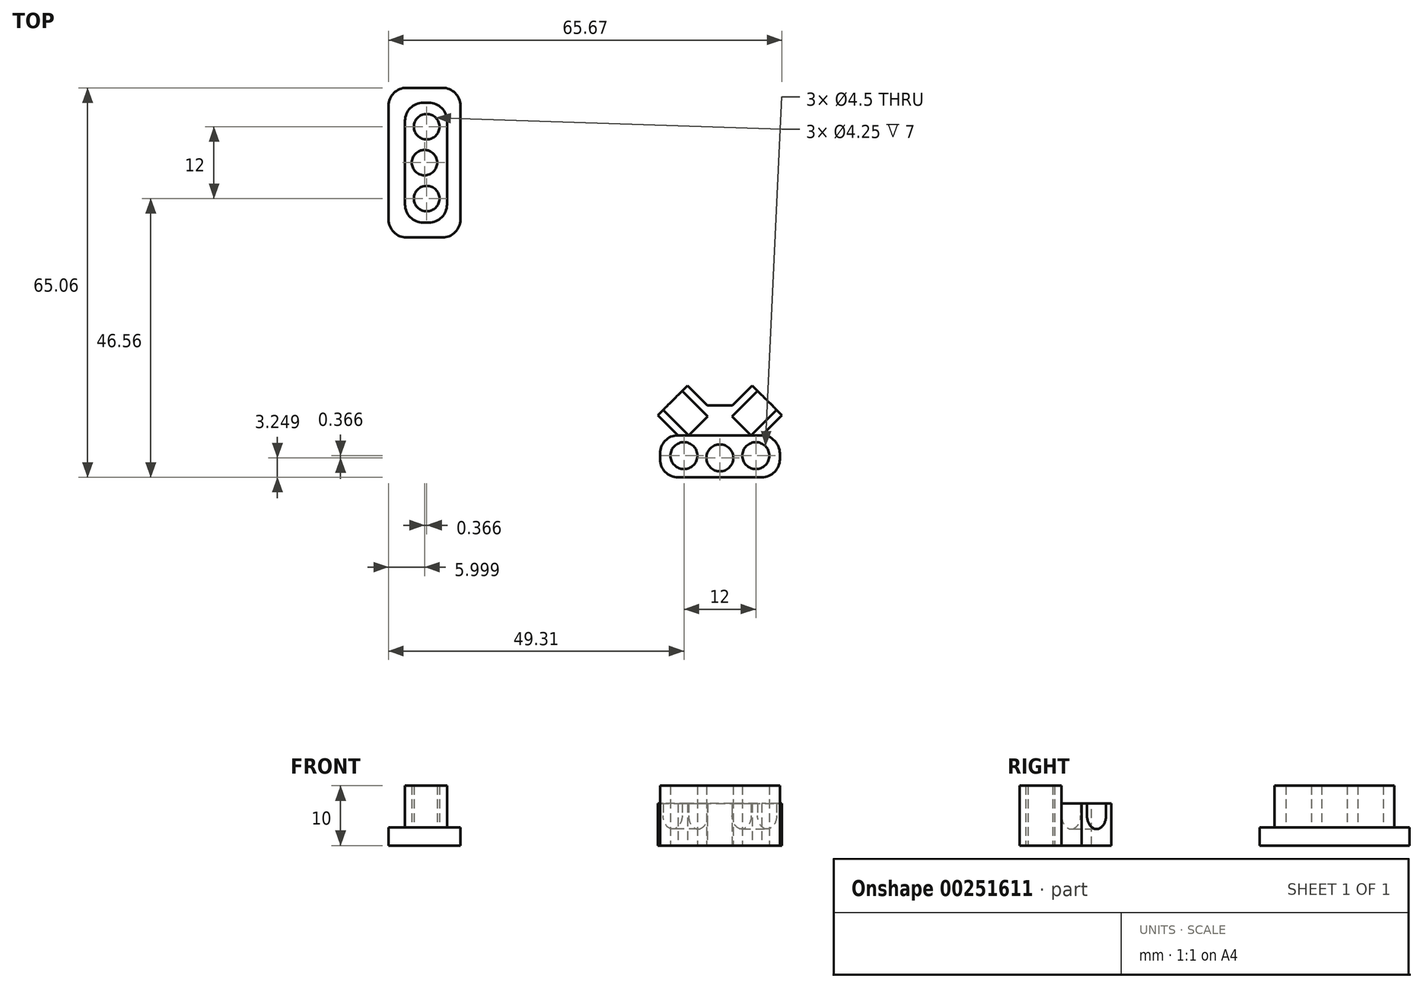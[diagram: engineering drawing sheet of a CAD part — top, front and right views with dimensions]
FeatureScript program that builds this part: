
annotation { "Feature Type Name" : "Feature", "Feature Type Description" : "" }
export const myFeature = defineFeature(function(context is Context, id is Id, definition is map)
    precondition{}
    {
        {
            var Q0;
            Q0=qCreatedBy(makeId("Top.planeOp"),FACE);
            var sketch = newSketch(context, id + "F0", { "sketchPlane" : qUnion([Q0])});
            skCircle(sketch, "E0.cCircle", {"center": v(0, 0) * mm, "radius": 49.31 * mm, "construction": true});
            skLineSegment(sketch, "E0.0", {"start": v(-45.56, 18.87) * mm, "end": v(-18.87, 45.56) * mm, "construction": true});
            skLineSegment(sketch, "E0.1", {"start": v(-18.87, 45.56) * mm, "end": v(18.87, 45.56) * mm, "construction": true});
            skLineSegment(sketch, "E0.2", {"start": v(18.87, 45.56) * mm, "end": v(45.56, 18.87) * mm, "construction": true});
            skLineSegment(sketch, "E0.3", {"start": v(45.56, 18.87) * mm, "end": v(45.56, -18.87) * mm, "construction": true});
            skLineSegment(sketch, "E0.4", {"start": v(45.56, -18.87) * mm, "end": v(18.87, -45.56) * mm, "construction": true});
            skLineSegment(sketch, "E0.5", {"start": v(18.87, -45.56) * mm, "end": v(-18.87, -45.56) * mm, "construction": true});
            skLineSegment(sketch, "E0.6", {"start": v(-18.87, -45.56) * mm, "end": v(-45.56, -18.87) * mm, "construction": true});
            skLineSegment(sketch, "E0.7", {"start": v(-45.56, -18.87) * mm, "end": v(-45.56, 18.87) * mm, "construction": true});
            skLineSegment(sketch, "E1.bottom", {"start": v(-48.56, -10) * mm, "end": v(-49.56, -10) * mm});
            skLineSegment(sketch, "E1.top", {"start": v(-48.56, 10) * mm, "end": v(-49.56, 10) * mm});
            skLineSegment(sketch, "E1.left", {"start": v(-45.56, -7) * mm, "end": v(-45.56, 7) * mm});
            skLineSegment(sketch, "E1.right", {"start": v(-52.56, -7) * mm, "end": v(-52.56, 7) * mm});
            skCircle(sketch, "E2", {"center": v(0, 0) * mm, "radius": 53.5 * mm, "construction": true});
            skCircle(sketch, "E3", {"center": v(-49.31, 0) * mm, "radius": 2.12 * mm});
            skCircle(sketch, "E4", {"center": v(-48.94, 6) * mm, "radius": 2.12 * mm});
            skCircle(sketch, "E5", {"center": v(-48.94, -6) * mm, "radius": 2.12 * mm});
            skPoint(sketch, "E6.visualSharp", {"position": v(-52.56, 10) * mm});
            skArc(sketch, "E6.filletArc", {"start": v(-49.56, 10) * mm, "mid": v(-51.68, 9.12) * mm, "end": v(-52.56, 7) * mm});
            skPoint(sketch, "E7.visualSharp", {"position": v(-45.56, 10) * mm});
            skArc(sketch, "E7.filletArc", {"start": v(-45.56, 7) * mm, "mid": v(-46.44, 9.12) * mm, "end": v(-48.56, 10) * mm});
            skPoint(sketch, "E8.visualSharp", {"position": v(-45.56, -10) * mm});
            skArc(sketch, "E8.filletArc", {"start": v(-48.56, -10) * mm, "mid": v(-46.44, -9.12) * mm, "end": v(-45.56, -7) * mm});
            skPoint(sketch, "E9.visualSharp", {"position": v(-52.56, -10) * mm});
            skArc(sketch, "E9.filletArc", {"start": v(-52.56, -7) * mm, "mid": v(-51.68, -9.12) * mm, "end": v(-49.56, -10) * mm});
            skLineSegment(sketch, "E10.bottom", {"start": v(-52.31, 12.5) * mm, "end": v(-46.31, 12.5) * mm});
            skLineSegment(sketch, "E10.top", {"start": v(-52.31, -12.5) * mm, "end": v(-46.31, -12.5) * mm});
            skLineSegment(sketch, "E10.left", {"start": v(-55.31, 9.5) * mm, "end": v(-55.31, -9.5) * mm});
            skLineSegment(sketch, "E10.right", {"start": v(-43.31, 9.5) * mm, "end": v(-43.31, -9.5) * mm});
            skPoint(sketch, "E11.visualSharp", {"position": v(-55.31, 12.5) * mm});
            skArc(sketch, "E11.filletArc", {"start": v(-52.31, 12.5) * mm, "mid": v(-54.43, 11.62) * mm, "end": v(-55.31, 9.5) * mm});
            skPoint(sketch, "E12.visualSharp", {"position": v(-43.31, 12.5) * mm});
            skArc(sketch, "E12.filletArc", {"start": v(-43.31, 9.5) * mm, "mid": v(-44.19, 11.62) * mm, "end": v(-46.31, 12.5) * mm});
            skPoint(sketch, "E13.visualSharp", {"position": v(-43.31, -12.5) * mm});
            skArc(sketch, "E13.filletArc", {"start": v(-46.31, -12.5) * mm, "mid": v(-44.19, -11.62) * mm, "end": v(-43.31, -9.5) * mm});
            skPoint(sketch, "E14.visualSharp", {"position": v(-55.31, -12.5) * mm});
            skArc(sketch, "E14.filletArc", {"start": v(-55.31, -9.5) * mm, "mid": v(-54.43, -11.62) * mm, "end": v(-52.31, -12.5) * mm});
            skLineSegment(sketch, "E15.bottom", {"start": v(49.56, -10) * mm, "end": v(48.56, -10) * mm});
            skLineSegment(sketch, "E15.top", {"start": v(49.56, 10) * mm, "end": v(48.56, 10) * mm});
            skLineSegment(sketch, "E15.left", {"start": v(52.56, -7) * mm, "end": v(52.56, 7) * mm});
            skLineSegment(sketch, "E15.right", {"start": v(45.56, -7) * mm, "end": v(45.56, 7) * mm});
            skCircle(sketch, "E16", {"center": v(49.31, 0) * mm, "radius": 2.25 * mm});
            skCircle(sketch, "E17", {"center": v(48.94, 6) * mm, "radius": 2.25 * mm});
            skCircle(sketch, "E18", {"center": v(48.94, -6) * mm, "radius": 2.25 * mm});
            skPoint(sketch, "E19.visualSharp", {"position": v(45.56, 10) * mm});
            skArc(sketch, "E19.filletArc", {"start": v(48.56, 10) * mm, "mid": v(46.44, 9.12) * mm, "end": v(45.56, 7) * mm});
            skPoint(sketch, "E20.visualSharp", {"position": v(52.56, 10) * mm});
            skArc(sketch, "E20.filletArc", {"start": v(52.56, 7) * mm, "mid": v(51.68, 9.12) * mm, "end": v(49.56, 10) * mm});
            skPoint(sketch, "E21.visualSharp", {"position": v(52.56, -10) * mm});
            skArc(sketch, "E21.filletArc", {"start": v(49.56, -10) * mm, "mid": v(51.68, -9.12) * mm, "end": v(52.56, -7) * mm});
            skPoint(sketch, "E22.visualSharp", {"position": v(45.56, -10) * mm});
            skArc(sketch, "E22.filletArc", {"start": v(45.56, -7) * mm, "mid": v(46.44, -9.12) * mm, "end": v(48.56, -10) * mm});
            skLineSegment(sketch, "E23.bottom", {"start": v(-7, -45.56) * mm, "end": v(7, -45.56) * mm});
            skLineSegment(sketch, "E23.top", {"start": v(-7, -52.56) * mm, "end": v(7, -52.56) * mm});
            skLineSegment(sketch, "E23.left", {"start": v(-10, -48.56) * mm, "end": v(-10, -49.56) * mm});
            skLineSegment(sketch, "E23.right", {"start": v(10, -48.56) * mm, "end": v(10, -49.56) * mm});
            skPoint(sketch, "E23.middle", {"position": v(0, -49.06) * mm});
            skPoint(sketch, "E24.visualSharp", {"position": v(-10, -52.56) * mm});
            skArc(sketch, "E24.filletArc", {"start": v(-10, -49.56) * mm, "mid": v(-9.12, -51.68) * mm, "end": v(-7, -52.56) * mm});
            skPoint(sketch, "E25.visualSharp", {"position": v(10, -52.56) * mm});
            skArc(sketch, "E25.filletArc", {"start": v(7, -52.56) * mm, "mid": v(9.12, -51.68) * mm, "end": v(10, -49.56) * mm});
            skPoint(sketch, "E26.visualSharp", {"position": v(10, -45.56) * mm});
            skArc(sketch, "E26.filletArc", {"start": v(10, -48.56) * mm, "mid": v(9.12, -46.44) * mm, "end": v(7, -45.56) * mm});
            skPoint(sketch, "E27.visualSharp", {"position": v(-10, -45.56) * mm});
            skArc(sketch, "E27.filletArc", {"start": v(-7, -45.56) * mm, "mid": v(-9.12, -46.44) * mm, "end": v(-10, -48.56) * mm});
            skCircle(sketch, "E28", {"center": v(0, -49.31) * mm, "radius": 2.25 * mm});
            skCircle(sketch, "E29", {"center": v(6, -48.94) * mm, "radius": 2.25 * mm});
            skCircle(sketch, "E30", {"center": v(-6, -48.94) * mm, "radius": 2.25 * mm});
            skLineSegment(sketch, "E31", {"start": v(7, -45.56) * mm, "end": v(45.56, -7) * mm, "construction": true});
            skLineSegment(sketch, "E32", {"start": v(7, -45.56) * mm, "end": v(-2.9, -45.56) * mm});
            skLineSegment(sketch, "E33", {"start": v(0, -42.66) * mm, "end": v(5.4, -37.25) * mm});
            skLineSegment(sketch, "E34", {"start": v(5.4, -37.25) * mm, "end": v(10.36, -42.2) * mm});
            skLineSegment(sketch, "E35", {"start": v(10.36, -42.2) * mm, "end": v(7, -45.56) * mm});
            skLineSegment(sketch, "E36", {"start": v(6.3, -38.13) * mm, "end": v(2.05, -42.38) * mm});
            skLineSegment(sketch, "E37", {"start": v(2.05, -42.38) * mm, "end": v(5.23, -45.56) * mm});
            skLineSegment(sketch, "E38", {"start": v(5.23, -45.56) * mm, "end": v(9.47, -41.31) * mm});
            skLineSegment(sketch, "E39.MirrorCS", {"start": v(-5.4, -37.25) * mm, "end": v(-10.36, -42.2) * mm});
            skLineSegment(sketch, "E40.MirrorCS", {"start": v(-6.3, -38.13) * mm, "end": v(-2.05, -42.38) * mm});
            skLineSegment(sketch, "E41.MirrorCS", {"start": v(-10.36, -42.2) * mm, "end": v(-7, -45.56) * mm});
            skLineSegment(sketch, "E42.MirrorCS", {"start": v(0, -42.66) * mm, "end": v(-5.4, -37.25) * mm});
            skLineSegment(sketch, "E43.MirrorCS", {"start": v(-7, -45.56) * mm, "end": v(-45.56, -7) * mm, "construction": true});
            skLineSegment(sketch, "E44.MirrorCS", {"start": v(-5.23, -45.56) * mm, "end": v(-9.47, -41.31) * mm});
            skLineSegment(sketch, "E45.MirrorCS", {"start": v(-2.05, -42.38) * mm, "end": v(-5.23, -45.56) * mm});
            skPoint(sketch, "E46.orphan", {"position": v(2.9, -45.56) * mm});
            skSolve(sketch);
        }
        {
            var Q0;
            Q0=makeQuery(id+"F0.imprint","IMPRINT",FACE,{"disambiguationData":[TD([[makeQuery(id+"F0.imprint","IMPRINT",EDGE,{"derivedFrom":sQuery(id+"F0.wireOp",EDGE,"E1.bottom")}),-1.0]])]});
            extrude(context, id + "F1", {"entities" : qUnion([Q0]), "depth" : 10 * mm});
        }
        {
            var Q0;
            Q0=makeQuery(id+"F0.imprint","IMPRINT",FACE,{"disambiguationData":[TD([[makeQuery(id+"F0.imprint","IMPRINT",EDGE,{"derivedFrom":sQuery(id+"F0.wireOp",EDGE,"E1.bottom")}),1.0]])]});
            var Q1;
            Q1=makeQuery(id+"F0.imprint","IMPRINT",FACE,{"disambiguationData":[TD([[makeQuery(id+"F0.imprint","IMPRINT",EDGE,{"derivedFrom":sQuery(id+"F0.wireOp",EDGE,"E4")}),1.0]])]});
            var Q2;
            Q2=makeQuery(id+"F0.imprint","IMPRINT",FACE,{"disambiguationData":[TD([[makeQuery(id+"F0.imprint","IMPRINT",EDGE,{"derivedFrom":sQuery(id+"F0.wireOp",EDGE,"E3")}),1.0]])]});
            var Q3;
            Q3=makeQuery(id+"F0.imprint","IMPRINT",FACE,{"disambiguationData":[TD([[makeQuery(id+"F0.imprint","IMPRINT",EDGE,{"derivedFrom":sQuery(id+"F0.wireOp",EDGE,"E5")}),1.0]])]});
            extrude(context, id + "F2", {"entities" : qUnion([Q0, Q1, Q2, Q3]), "operationType" : NewBodyOperationType.ADD, "depth" : 3 * mm});
        }
        {
            var Q0;
            Q0=makeQuery(id+"F0.imprint","IMPRINT",FACE,{"disambiguationData":[TD([[makeQuery(id+"F0.imprint","IMPRINT",EDGE,{"derivedFrom":sQuery(id+"F0.wireOp",EDGE,"E23.top")}),1.0]])]});
            extrude(context, id + "F3", {"entities" : qUnion([Q0]), "depth" : 10 * mm});
        }
        {
            var Q0;
            {var subQ1=sQuery(id+"F0.wireOp",EDGE,"E33");Q0=makeQuery(id+"F0.imprint","IMPRINT",FACE,{"disambiguationData":[TD([[makeQuery(id+"F0.imprint","IMPRINT",EDGE,{"derivedFrom":subQ1}),-1.0]])]});}
            var Q1;
            {var subQ0=sQuery(id+"F0.wireOp",EDGE,"E35");Q1=makeQuery(id+"F0.imprint","IMPRINT",FACE,{"disambiguationData":[TD([[makeQuery(id+"F0.imprint","IMPRINT",EDGE,{"derivedFrom":subQ0}),-1.0]])]});}
            var Q2;
            {var subQ0=sQuery(id+"F0.wireOp",EDGE,"E41.MirrorCS");Q2=makeQuery(id+"F0.imprint","IMPRINT",FACE,{"disambiguationData":[TD([[makeQuery(id+"F0.imprint","IMPRINT",EDGE,{"derivedFrom":subQ0}),1.0]])]});}
            extrude(context, id + "F4", {"entities" : qUnion([Q0, Q1, Q2]), "depth" : 7 * mm});
        }
        {
            var Q0;
            {var subQ0=sQuery(id+"F0.wireOp",EDGE,"E40.MirrorCS");Q0=makeQuery(id+"F0.imprint","IMPRINT",FACE,{"disambiguationData":[TD([[makeQuery(id+"F0.imprint","IMPRINT",EDGE,{"derivedFrom":subQ0}),-1.0]])]});}
            var Q1;
            Q1=makeQuery(id+"F0.imprint","IMPRINT",FACE,{"disambiguationData":[TD([[makeQuery(id+"F0.imprint","IMPRINT",EDGE,{"derivedFrom":sQuery(id+"F0.wireOp",EDGE,"E37")}),1.0]])]});
            extrude(context, id + "F5", {"entities" : qUnion([Q0, Q1]), "depth" : 5 * mm});
        }
        {
            var Q0;
            Q0=makeQuery(id+"F3.opExtrude","SWEPT_BODY",BODY,{"disambiguationData":[OSD([sQuery(id+"F0.wireOp",EDGE,"E23.bottom"),sQuery(id+"F0.wireOp",EDGE,"E23.top"),sQuery(id+"F0.wireOp",EDGE,"E23.left"),sQuery(id+"F0.wireOp",EDGE,"E23.right"),sQuery(id+"F0.wireOp",EDGE,"E24.filletArc"),sQuery(id+"F0.wireOp",EDGE,"E25.filletArc"),sQuery(id+"F0.wireOp",EDGE,"E26.filletArc"),sQuery(id+"F0.wireOp",EDGE,"E27.filletArc"),sQuery(id+"F0.wireOp",EDGE,"E28"),sQuery(id+"F0.wireOp",EDGE,"E29"),sQuery(id+"F0.wireOp",EDGE,"E30"),sQuery(id+"F0.wireOp",EDGE,"E32")])]});
            var Q1;
            Q1=makeQuery(id+"F5.opExtrude","SWEPT_BODY",BODY,{"disambiguationData":[OSD([sQuery(id+"F0.wireOp",EDGE,"E40.MirrorCS"),sQuery(id+"F0.wireOp",EDGE,"E39.MirrorCS"),sQuery(id+"F0.wireOp",EDGE,"E44.MirrorCS"),sQuery(id+"F0.wireOp",EDGE,"E45.MirrorCS")])]});
            var Q2;
            Q2=makeQuery(id+"F4.opExtrude","SWEPT_BODY",BODY,{"disambiguationData":[OSD([sQuery(id+"F0.wireOp",EDGE,"E23.bottom"),sQuery(id+"F0.wireOp",EDGE,"E32"),sQuery(id+"F0.wireOp",EDGE,"E33"),sQuery(id+"F0.wireOp",EDGE,"E34"),sQuery(id+"F0.wireOp",EDGE,"E37"),sQuery(id+"F0.wireOp",EDGE,"E36"),sQuery(id+"F0.wireOp",EDGE,"E40.MirrorCS"),sQuery(id+"F0.wireOp",EDGE,"E39.MirrorCS"),sQuery(id+"F0.wireOp",EDGE,"E42.MirrorCS"),sQuery(id+"F0.wireOp",EDGE,"E45.MirrorCS")])]});
            var Q3;
            Q3=makeQuery(id+"F4.opExtrude","SWEPT_BODY",BODY,{"disambiguationData":[OSD([sQuery(id+"F0.wireOp",EDGE,"E23.bottom"),sQuery(id+"F0.wireOp",EDGE,"E41.MirrorCS"),sQuery(id+"F0.wireOp",EDGE,"E39.MirrorCS"),sQuery(id+"F0.wireOp",EDGE,"E44.MirrorCS")])]});
            var Q4;
            Q4=makeQuery(id+"F5.opExtrude","SWEPT_BODY",BODY,{"disambiguationData":[OSD([sQuery(id+"F0.wireOp",EDGE,"E34"),sQuery(id+"F0.wireOp",EDGE,"E37"),sQuery(id+"F0.wireOp",EDGE,"E38"),sQuery(id+"F0.wireOp",EDGE,"E36")])]});
            var Q5;
            Q5=makeQuery(id+"F4.opExtrude","SWEPT_BODY",BODY,{"disambiguationData":[OSD([sQuery(id+"F0.wireOp",EDGE,"E32"),sQuery(id+"F0.wireOp",EDGE,"E34"),sQuery(id+"F0.wireOp",EDGE,"E35"),sQuery(id+"F0.wireOp",EDGE,"E38")])]});
            booleanBodies(context, id + "F6", {"operationType" : BooleanOperationType.UNION, "tools" : qUnion([Q0, Q1, Q2, Q3, Q4, Q5])});
        }
        {
            var Q0;
            {var subQ0=sQuery(id+"F0.wireOp",EDGE,"E34");Q0=makeQuery(id+"F6.opBoolean","MERGE",FACE,{"derivedFrom":[makeQuery(id+"F4.opExtrude","SWEPT_FACE",FACE,{"disambiguationData":[OSD([subQ0]),TDD([makeQuery(id+"F0.imprint","IMPRINT",EDGE,{"disambiguationData":[TD([[makeQuery(id+"F0.imprint","INTERSECT",VERTEX,{"derivedFrom":[sQuery(id+"F0.wireOp",EDGE,"E33"),subQ0]}),-1.0]])],"derivedFrom":subQ0})])]}),makeQuery(id+"F4.opExtrude","SWEPT_FACE",FACE,{"disambiguationData":[OSD([subQ0]),TDD([makeQuery(id+"F0.imprint","IMPRINT",EDGE,{"disambiguationData":[TD([[makeQuery(id+"F0.imprint","INTERSECT",VERTEX,{"derivedFrom":[subQ0,sQuery(id+"F0.wireOp",EDGE,"E35")]}),1.0]])],"derivedFrom":subQ0})])]}),makeQuery(id+"F5.opExtrude","SWEPT_FACE",FACE,{"disambiguationData":[OSD([subQ0])]})]});}
            var sketch = newSketch(context, id + "F7", { "sketchPlane" : qUnion([Q0])});
            skArc(sketch, "E47", {"start": v(-35.91, 5) * mm, "mid": v(-33.66, 2.75) * mm, "end": v(-31.41, 5) * mm});
            skLineSegment(sketch, "E48", {"start": v(-35.91, 5) * mm, "end": v(-31.41, 5) * mm});
            skSolve(sketch);
        }
        {
            var Q0;
            Q0=makeQuery(id+"F7.imprint","IMPRINT",FACE,{"disambiguationData":[TD([[makeQuery(id+"F7.imprint","IMPRINT",EDGE,{"derivedFrom":sQuery(id+"F7.wireOp",EDGE,"E47")}),1.0]])]});
            var Q1;
            Q1=makeQuery(id+"F4.opExtrude","SWEPT_FACE",FACE,{"disambiguationData":[OSD([sQuery(id+"F0.wireOp",EDGE,"E37")])]});
            extrude(context, id + "F8", {"entities" : qUnion([Q0]), "operationType" : NewBodyOperationType.REMOVE, "endBound" : BoundingType.UP_TO_SURFACE, "oppositeDirection" : true, "endBoundEntityFace" : qUnion([Q1]), "depth" : 25 * mm});
        }
        {
            var Q0;
            {var subQ0=sQuery(id+"F0.wireOp",EDGE,"E39.MirrorCS");Q0=makeQuery(id+"F6.opBoolean","MERGE",FACE,{"derivedFrom":[makeQuery(id+"F4.opExtrude","SWEPT_FACE",FACE,{"disambiguationData":[OSD([subQ0]),TDD([makeQuery(id+"F0.imprint","IMPRINT",EDGE,{"disambiguationData":[TD([[makeQuery(id+"F0.imprint","INTERSECT",VERTEX,{"derivedFrom":[sQuery(id+"F0.wireOp",EDGE,"E40.MirrorCS"),subQ0]}),1.0]])],"derivedFrom":subQ0})])]}),makeQuery(id+"F4.opExtrude","SWEPT_FACE",FACE,{"disambiguationData":[OSD([subQ0]),TDD([makeQuery(id+"F0.imprint","IMPRINT",EDGE,{"disambiguationData":[TD([[makeQuery(id+"F0.imprint","INTERSECT",VERTEX,{"derivedFrom":[sQuery(id+"F0.wireOp",EDGE,"E41.MirrorCS"),subQ0]}),1.0]])],"derivedFrom":subQ0})])]}),makeQuery(id+"F5.opExtrude","SWEPT_FACE",FACE,{"disambiguationData":[OSD([subQ0])]})]});}
            var sketch = newSketch(context, id + "F9", { "sketchPlane" : qUnion([Q0])});
            skArc(sketch, "E49", {"start": v(31.41, 5) * mm, "mid": v(33.66, 2.75) * mm, "end": v(35.91, 5) * mm});
            skSolve(sketch);
        }
        {
            var Q0;
            Q0=makeQuery(id+"F9.imprint","IMPRINT",FACE,{"disambiguationData":[TD([[makeQuery(id+"F9.imprint","IMPRINT",EDGE,{"derivedFrom":sQuery(id+"F9.wireOp",EDGE,"E49")}),1.0]])]});
            var Q1;
            Q1=makeQuery(id+"F4.opExtrude","SWEPT_FACE",FACE,{"disambiguationData":[OSD([sQuery(id+"F0.wireOp",EDGE,"E45.MirrorCS")])]});
            extrude(context, id + "F10", {"entities" : qUnion([Q0]), "operationType" : NewBodyOperationType.REMOVE, "endBound" : BoundingType.UP_TO_SURFACE, "oppositeDirection" : true, "endBoundEntityFace" : qUnion([Q1]), "depth" : 25 * mm});
        }
        {
            var Q0;
            Q0=makeQuery(id+"F4.opExtrude","SWEPT_EDGE",EDGE,{"disambiguationData":[OSD([sQuery(id+"F0.wireOp",EDGE,"E33"),sQuery(id+"F0.wireOp",EDGE,"E42.MirrorCS")])]});
            chamfer(context, id + "F11", {"entities" : qUnion([Q0]), "width" : 3 * mm, "tangentPropagation" : true});
        }
    });
